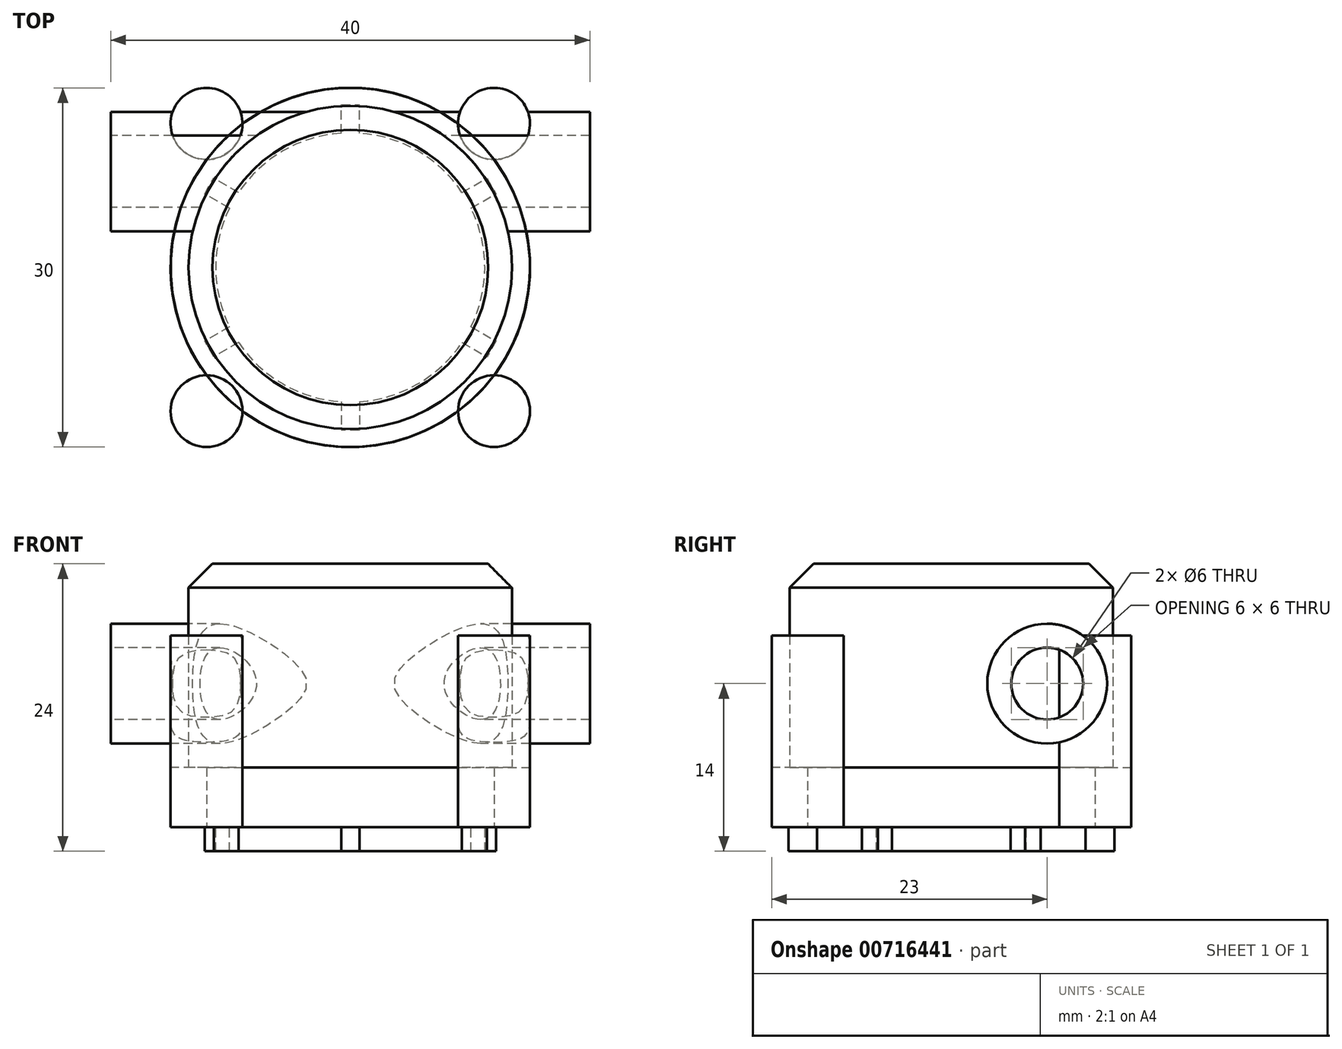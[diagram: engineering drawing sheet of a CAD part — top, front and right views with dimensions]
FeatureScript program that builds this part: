
annotation { "Feature Type Name" : "Feature", "Feature Type Description" : "" }
export const myFeature = defineFeature(function(context is Context, id is Id, definition is map)
    precondition{}
    {
        {
            var Q0;
            Q0=qCreatedBy(makeId("Top.planeOp"),FACE);
            var sketch = newSketch(context, id + "F0", { "sketchPlane" : qUnion([Q0])});
            skLineSegment(sketch, "E0", {"start": v(0, -30.4) * mm, "end": v(0, 42.81) * mm, "construction": true});
            skLineSegment(sketch, "E1", {"start": v(-43.65, 0) * mm, "end": v(49.75, 0) * mm, "construction": true});
            skCircle(sketch, "E2", {"center": v(0, 0) * mm, "radius": 15 * mm});
            skSolve(sketch);
        }
        {
            var Q0;
            Q0=qSketchRegion(id+"F0",true);
            extrude(context, id + "F1", {"entities" : qUnion([Q0]), "depth" : 5 * mm, "offsetDistance" : 25 * mm});
        }
        {
            var Q0;
            Q0=makeQuery(id+"F1.opExtrude","CAP_FACE",FACE,{"disambiguationData":[OSD([sQuery(id+"F0.wireOp",EDGE,"E2")])],"isStart":true});
            var sketch = newSketch(context, id + "F2", { "sketchPlane" : qUnion([Q0])});
            skCircle(sketch, "E3", {"center": v(12, -12) * mm, "radius": 3 * mm});
            skCircle(sketch, "E4.MirrorC", {"center": v(-12, -12) * mm, "radius": 3 * mm});
            skCircle(sketch, "E5.MirrorC", {"center": v(-12, 12) * mm, "radius": 3 * mm});
            skCircle(sketch, "E6.MirrorC", {"center": v(12, 12) * mm, "radius": 3 * mm});
            skSolve(sketch);
        }
        {
            var Q0;
            Q0=qSketchRegion(id+"F2",true);
            extrude(context, id + "F3", {"entities" : qUnion([Q0]), "operationType" : NewBodyOperationType.ADD, "oppositeDirection" : true, "depth" : 16 * mm, "offsetDistance" : 25 * mm});
        }
        {
            var Q0;
            Q0=qCreatedBy(makeId("Front.planeOp"),FACE);
            var sketch = newSketch(context, id + "F4", { "sketchPlane" : qUnion([Q0])});
            skLineSegment(sketch, "E7", {"start": v(0, 31.61) * mm, "end": v(0, -24.43) * mm, "construction": true});
            skSolve(sketch);
        }
        {
            var Q0;
            Q0=qCreatedBy(makeId("Right.planeOp"),FACE);
            var sketch = newSketch(context, id + "F5", { "sketchPlane" : qUnion([Q0])});
            skCircle(sketch, "E8", {"center": v(8, 12) * mm, "radius": 5 * mm});
            skCircle(sketch, "E9", {"center": v(8, 12) * mm, "radius": 3 * mm});
            skSolve(sketch);
        }
        {
            var Q0;
            Q0=makeQuery(id+"F1.opExtrude","CAP_FACE",FACE,{"disambiguationData":[OSD([sQuery(id+"F0.wireOp",EDGE,"E2")])],"isStart":false});
            var sketch = newSketch(context, id + "F6", { "sketchPlane" : qUnion([Q0])});
            skCircle(sketch, "E10", {"center": v(0, 0) * mm, "radius": 13.5 * mm});
            skSolve(sketch);
        }
        {
            var Q0;
            Q0 = qSketchRegion(id + "F6", true);
            extrude(context, id + "F7", {"entities" : qUnion([Q0]), "operationType" : NewBodyOperationType.ADD, "depth" : 17 * mm, "offsetDistance" : 25 * mm});
        }
        {
            var Q0;
            Q0=makeQuery(id+"F7.opExtrude","CAP_EDGE",EDGE,{"disambiguationData":[OSD([sQuery(id+"F6.wireOp",EDGE,"E10")])],"isStart":false});
            chamfer(context, id + "F8", {"entities" : qUnion([Q0]), "width" : 2 * mm, "tangentPropagation" : true});
        }
        {
            var Q0;
            Q0 = qSketchRegion(id + "F5", true);
            extrude(context, id + "F9", {"entities" : qUnion([Q0]), "operationType" : NewBodyOperationType.ADD, "depth" : 40 * mm, "offsetDistance" : 25 * mm, "symmetric" : true});
        }
        {
            var Q0;
            Q0=makeQuery(id+"F3.boolean.opBoolean","MERGE",FACE,{"derivedFrom":[makeQuery(id+"F1.opExtrude","CAP_FACE",FACE,{"disambiguationData":[OSD([sQuery(id+"F0.wireOp",EDGE,"E2")])],"isStart":true}),makeQuery(id+"F3.opExtrude","CAP_FACE",FACE,{"disambiguationData":[OSD([sQuery(id+"F2.wireOp",EDGE,"E3")])],"isStart":true}),makeQuery(id+"F3.opExtrude","CAP_FACE",FACE,{"disambiguationData":[OSD([sQuery(id+"F2.wireOp",EDGE,"E4.MirrorC")])],"isStart":true}),makeQuery(id+"F3.opExtrude","CAP_FACE",FACE,{"disambiguationData":[OSD([sQuery(id+"F2.wireOp",EDGE,"E5.MirrorC")])],"isStart":true}),makeQuery(id+"F3.opExtrude","CAP_FACE",FACE,{"disambiguationData":[OSD([sQuery(id+"F2.wireOp",EDGE,"E6.MirrorC")])],"isStart":true})]});
            var sketch = newSketch(context, id + "F10", { "sketchPlane" : qUnion([Q0])});
            skArc(sketch, "E11", {"start": v(0.76, -11.2) * mm, "mid": v(5.62, -9.73) * mm, "end": v(9.33, -6.26) * mm});
            skLineSegment(sketch, "E12.top", {"start": v(-0.76, -13.6) * mm, "end": v(0.76, -13.6) * mm});
            skLineSegment(sketch, "E12.left", {"start": v(-0.76, -11.2) * mm, "end": v(-0.76, -13.6) * mm});
            skLineSegment(sketch, "E12.right", {"start": v(0.76, -11.2) * mm, "end": v(0.76, -13.6) * mm});
            skPoint(sketch, "E12.middle", {"position": v(0, -11.24) * mm});
            skPoint(sketch, "E13.1.0", {"position": v(9.73, -5.62) * mm});
            skLineSegment(sketch, "E13.1.2", {"start": v(9.33, -6.26) * mm, "end": v(11.4, -7.46) * mm});
            skLineSegment(sketch, "E13.1.3", {"start": v(11.4, -7.46) * mm, "end": v(12.16, -6.14) * mm});
            skLineSegment(sketch, "E13.1.4", {"start": v(10.09, -4.95) * mm, "end": v(12.16, -6.14) * mm});
            skPoint(sketch, "E13.2.0", {"position": v(9.73, 5.62) * mm});
            skLineSegment(sketch, "E13.2.2", {"start": v(10.09, 4.95) * mm, "end": v(12.16, 6.14) * mm});
            skLineSegment(sketch, "E13.2.3", {"start": v(12.16, 6.14) * mm, "end": v(11.4, 7.46) * mm});
            skLineSegment(sketch, "E13.2.4", {"start": v(9.33, 6.26) * mm, "end": v(11.4, 7.46) * mm});
            skPoint(sketch, "E13.3.0", {"position": v(0, 11.24) * mm});
            skLineSegment(sketch, "E13.3.2", {"start": v(0.76, 11.2) * mm, "end": v(0.76, 13.6) * mm});
            skLineSegment(sketch, "E13.3.3", {"start": v(0.76, 13.6) * mm, "end": v(-0.76, 13.6) * mm});
            skLineSegment(sketch, "E13.3.4", {"start": v(-0.76, 11.2) * mm, "end": v(-0.76, 13.6) * mm});
            skPoint(sketch, "E13.4.0", {"position": v(-9.73, 5.62) * mm});
            skLineSegment(sketch, "E13.4.2", {"start": v(-9.33, 6.26) * mm, "end": v(-11.4, 7.46) * mm});
            skLineSegment(sketch, "E13.4.3", {"start": v(-11.4, 7.46) * mm, "end": v(-12.16, 6.14) * mm});
            skLineSegment(sketch, "E13.4.4", {"start": v(-10.09, 4.95) * mm, "end": v(-12.16, 6.14) * mm});
            skPoint(sketch, "E13.5.0", {"position": v(-9.73, -5.62) * mm});
            skLineSegment(sketch, "E13.5.2", {"start": v(-10.09, -4.95) * mm, "end": v(-12.16, -6.14) * mm});
            skLineSegment(sketch, "E13.5.3", {"start": v(-12.16, -6.14) * mm, "end": v(-11.4, -7.46) * mm});
            skLineSegment(sketch, "E13.5.4", {"start": v(-9.33, -6.26) * mm, "end": v(-11.4, -7.46) * mm});
            skPoint(sketch, "E12.bottom.end.orphan", {"position": v(0.76, -8.87) * mm});
            skPoint(sketch, "E14.orphan", {"position": v(-0.76, -8.87) * mm});
            skArc(sketch, "E15.trimOffspring", {"start": v(-9.33, -6.26) * mm, "mid": v(-5.62, -9.73) * mm, "end": v(-0.76, -11.2) * mm});
            skPoint(sketch, "E16.orphan", {"position": v(-7.3, -5.1) * mm});
            skPoint(sketch, "E17.orphan", {"position": v(-7.3, 5.1) * mm});
            skArc(sketch, "E18.trimOffspring", {"start": v(-10.09, 4.95) * mm, "mid": v(-11.24, 0) * mm, "end": v(-10.09, -4.95) * mm});
            skArc(sketch, "E19.trimOffspring", {"start": v(-0.76, 11.2) * mm, "mid": v(-5.62, 9.73) * mm, "end": v(-9.33, 6.26) * mm});
            skArc(sketch, "E20.trimOffspring", {"start": v(9.33, 6.26) * mm, "mid": v(5.62, 9.73) * mm, "end": v(0.76, 11.2) * mm});
            skArc(sketch, "E21.trimOffspring", {"start": v(10.09, -4.95) * mm, "mid": v(11.24, 0) * mm, "end": v(10.09, 4.95) * mm});
            skPoint(sketch, "E22.orphan", {"position": v(7.3, -5.1) * mm});
            skPoint(sketch, "E23.orphan", {"position": v(8.06, 3.78) * mm});
            skPoint(sketch, "E24.orphan", {"position": v(-0.76, 8.87) * mm});
            skSolve(sketch);
        }
        {
            var Q0;
            Q0 = qSketchRegion(id + "F10", true);
            extrude(context, id + "F11", {"entities" : qUnion([Q0]), "operationType" : NewBodyOperationType.ADD, "depth" : 2 * mm, "offsetDistance" : 25 * mm});
        }
    });
